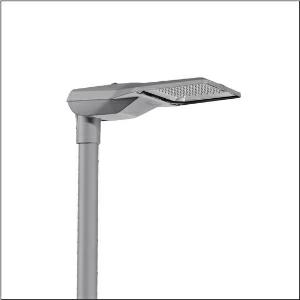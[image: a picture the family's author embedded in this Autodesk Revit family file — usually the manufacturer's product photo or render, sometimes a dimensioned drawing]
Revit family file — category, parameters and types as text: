
# Revit family: streetlight_sl_21_iq_midi___st1_0ab_5xe3m31v08nb_f534
name_source: partatom
category: Lighting Fixtures
units: mm (PartAtom-declared; Revit-internal decimal feet)

## family parameters
Cut with Voids When Loaded = No
Host = Face
Light Source = No
Part Type = Normal
Room Calculation Point = No
Round Connector Dimension = Use Diameter
Shared = No

## types (1)
- --- (1 x LED, 18970 lm, 136.6 W, 3000K)
    Apparent Load = 137 VA
    CIE Flux Codes = 40 74 97 100 100
    Color Rendering = 70
    Color Temperature = 3000K
    Default Elevation = 1800 mm
    Description = Streetlight SL 21 iQ midi, mast luminaire, primary light control with lens, of PMMA, primary optical cover: cover, of toughened safety glass, transparent, light distribution: ST1.0aB, light emission: direct distribution, primary light characteristic: asymmetric, installation type: post-top, side-entry, LED, High Power LED, rated luminous flux: 18.970lm, luminous efficacy: 139lm/W, light colour: 730, colour temperature: 3000K, control: presetting dimming logarithmic, Street-Remote, Auto-Match, Temp-Guard, Lumen-Switch, Night-Set, Smart-Wire, Light-Fading, Desk-Remote (wireless, voltage-free reading and setting of iQ features in the workshop via application-optimized NFC function/RFID function), optimised constant luminous flux control (CLO 2.0), mains connection: 230..240V, AC, 50/60Hz, start of lifetime: 137W, end of service life: 144W, reduction: 61W, luminaire housing, of diecast aluminium, powder-coated, Siteco® metallic grey (DB 702S), corrosivity category C5 mid according to DIN EN ISO 12944, please order mast flange separately, inclination adjustable: 0°, 5°, 10°, 15°, sealing non-destructively replaceable, multi-level sealing system, length: 644mm, width: 335mm, height: 110mm, mast flange for spigot size: 42mm (side-entry): 5XC10008XM4, 60/48mm (side-entry/post-top): 5XC10108XM2, 76/60mm (side-entry/post-top): 5XC10108XM1, Smart Interface above, protection rating (complete): IP66, insulation class (complete): insulation class II (safety insulation), certification: CE, ENEC, ENEC+, VDE, impact resistance: IK09, permissible operating ambient temperature for outdoor applications: -40..+50°C, standard-compliant lighting for roads and squares, packaging unit: 1 piece

Light Distribution: ST1.0aB
    Height = 111 mm
    Lamp = 1 x LED
    Lamp Light Flux = 18970 lm
    Lamp Power = 136.6 W
    Lamp count = 1
    Length = 644 mm
    Luminous efficacy = 139 lm/W
    Manufacturer = Siteco
    ModVariant = No
    Model = 5XE3M31V08NB
    Number of Poles = 1
    OnlyDefault = Yes
    Power Factor = 1
    Product Name = Streetlight SL 21 iQ midi | ST1.0aB
    Product group = mast luminaire | pylon top
    ProductGroupID = 6100
    Protection Class = Protection class II
    Protection Degree = IP 66
    RLX_Detail_Level = 1
    RLX_Emergency_Light_Flux = 0 lm
    RLX_Emergency_Type = 0
    RLX_Emergency_Type_DB = No
    RlxData = <blob elided: 90821 chars, md5=9e0db7a1>
    Socket = socket
    Standby Power = 0 W
    System Light Flux = 18970 lm
    System Power = 137 W
    Type Comments = factory setting: luminous flux: 100 % | dim-lin: 254 | 733 mA
    Type Image = l_1004302.jpg
    URL = http://relux.com
    VarID = @adj_060337
    Voltage = 0 V
    Weight = 0.00 kg
    Width = 336 mm

## geometry (parser evidence)
native form markers: Blend x4, Sweep x11
no freeform markers — native parametric forms only
